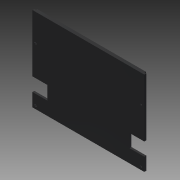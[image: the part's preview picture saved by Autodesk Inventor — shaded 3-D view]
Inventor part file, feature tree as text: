
AUTODESK INVENTOR PART (.ipt)
format: ipt  version: 2015 (Build 190159000, 159)  size: 178,688 bytes
history: native  units: mm
features: extrude x3, sketch x3
ambient origin geometry x8: Origin, YZ Plane, XZ Plane, XY Plane, X Axis, Y Axis, Z Axis, Center Point
bodies: Solid1 (feature_tree)
feature tree (6):
  extrude  "Extrusion1"  Depth=22.5mm
  extrude  "Extrusion2"  Depth=20.0mm
  extrude  "Extrusion4"  Depth=170.0mm
  sketch  "Sketch1"  dims[d0=88.0mm d2=22.5mm]
  sketch  "Sketch2"  dims[d3=22.5mm d4=20.0mm]
  sketch  "Sketch3"  dims[d5=20.0mm d6=170.0mm d7=3.0mm d8=0.0mm d9=6.5mm d10=4.5mm d11=4.5mm d12=2.5mm d13=2.5mm d16=2.0mm d17=0.0mm d23=5.5mm d24=5.5mm d25=5.5mm d26=5.5mm d27=3.0mm d28=3.0mm d33=6.0mm d34=5.0mm d35=0.0mm d36=3.0mm d43=5.5mm d48=2.75mm d49=2.5mm d55=5.0mm d56=2.5mm d57=6.5mm d58=4.5mm d59=4.5mm d60=2.5mm d61=3.0mm d62=3.0mm d63=3.0mm d64=22.5mm d65=22.5mm d66=170.0mm d67=2.0mm d69=41.5mm d72=41.5mm]
